# Revit family: 0051681 Feilo Sylvania Lighting Fixture SYLMASTER T8 LED 1200 HO 4K Pendant
name_source: partatom
category: Lighting Fixtures
revit_build: Autodesk Revit 2017 (Build: 20190507_1515(x64)
units: mm (PartAtom-declared; Revit-internal decimal feet)

## family parameters
Cut with Voids When Loaded = No
Host = Face
Light Source = Yes
OmniClass Number = 23.80.70.00
OmniClass Title = Lighting
Part Type = Normal
Room Calculation Point = No
Round Connector Dimension = Use Diameter
Shared = No

## types (1)
- 0051681 SYLMASTER T8 LED 1200 HO 4K
    Apparent Load = 40 VA
    Array_FEILO = 25
    Assembly Code = D5020200
    AssetType = Fixed
    ClassificationName = Uniclass2015
    ClassificationValue = EF_70_80
    Color Filter = 16777215
    Cost = 0 $
    Default Elevation = 1219 mm
    Description = SYLMASTER T8 LED 1200 HO 4K is a surface mount / pendant luminaire supplied with 2 ToLEDo T8 20W 840 LED Tubes.
    Dimming Lamp Color Temperature Shift = <None>
    DimmingControlOptions = Non dimmable
    DocumentationLiterature = http://www.sylvania-lighting.com
    DurationUnit = hours
    ElectricShockClassification = Class I
    Emit Shape Visible in Rendering = No
    Emit from Rectangle Length = 1220 mm  [stored 4.00262 ft]
    Emit from Rectangle Width = 160 mm  [stored 0.524934 ft]
    ExpectedLife = 50000
    IfcExportAs = IfcLightFixtureType
    IfcExportType = IfcLightFixtureType
    ImpactProtectionIndex = IK02
    IngressProtection = IP20
    InputNominalFrequency = 50/60 Hz
    InputVoltage = 220-240V~
    Keynote = 16500
    Lamp = LED
    LampColourRenderingIndex = 80
    LampColourTemperature = 4000 K
    LampMacAdamStep = 6
    LampNominalLuminous = 3040 lm
    LampsType = LED
    Length_FEILO = 1250 mm  [stored 4.10105 ft]
    LightOutputRatio = 71
    LuminousEfficacy = 76 lm/W
    Manufacturer = Feilo Sylvania
    ManufacturerName = Feilo Sylvania
    Material = steel housing
    Material_1_FEILO = Body-Sylvania-Sylmaster-White
    Material_2_FEILO = LEDTube-Sylvania-Sylmaster
    Material_3_FEILO = <By Category>
    Material_4_FEILO = <By Category>
    Model = SYLMASTER T8 LED 1200 HO 4K
    ModelNumber = 0051681
    ModelReference = SYLMASTER T8 LED 1200 HO 4K
    Name = SYLMASTER T8 LED 1200 HO 4K
    NominalDepth = 202 mm  [stored 0.66273 ft]
    NominalHeight = 85 mm
    NominalLength = 1250 mm  [stored 4.10105 ft]
    Photometric Web File = 0051681.ies
    PowerConsumption = 40 W
    PowerFactor = 0.9
    RadiusSuspensionSleeve_FEILO = 3 mm  [stored 0.00984252 ft]
    RadiusSuspensionWire_FEILO = 2 mm  [stored 0.00656168 ft]
    RadiusTube_FEILO = 13 mm
    ReflectorSpacing_FEILO = 51 mm
    Single_FEILO = No
    Tilt Angle = -90.00°
    Twin_FEILO = Yes
    Type Image = <None>
    TypeName = SYLMASTER T8 LED 1200 HO 4K
    URL = http://www.sylvania-lighting.com
    Voltage = 230 V
    Weight = 3.41 kg
    WidthVoid_FEILO = 160 mm  [stored 0.524934 ft]

note: [stored X ft] marks values corroborated as IEEE doubles in the binary element streams (Revit-internal decimal feet)

## geometry (parser evidence)
native form markers: Sweep x6
no freeform markers — native parametric forms only
